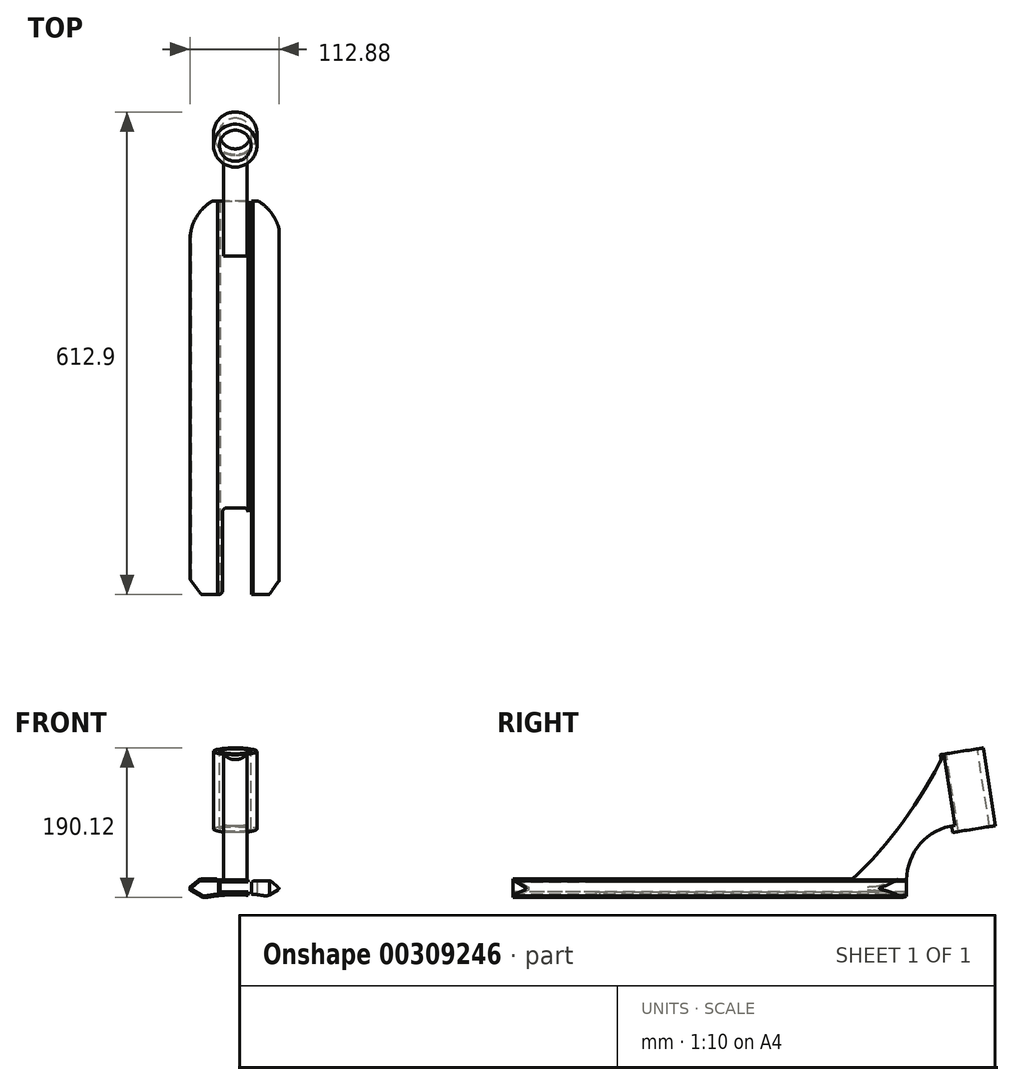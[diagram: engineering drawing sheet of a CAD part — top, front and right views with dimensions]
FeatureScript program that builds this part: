
annotation { "Feature Type Name" : "Feature", "Feature Type Description" : "" }
export const myFeature = defineFeature(function(context is Context, id is Id, definition is map)
    precondition{}
    {
        {
            var Q0;
            Q0=qCreatedBy(makeId("Front.planeOp"),FACE);
            var sketch = newSketch(context, id + "F0", { "sketchPlane" : qUnion([Q0])});
            skLineSegment(sketch, "E0", {"start": v(0, 0) * mm, "end": v(0, 5.19) * mm, "construction": true});
            skLineSegment(sketch, "E1", {"start": v(0, 3.89) * mm, "end": v(22.5, 3.89) * mm});
            skLineSegment(sketch, "E2", {"start": v(22.5, 3.89) * mm, "end": v(22.5, 5.19) * mm});
            skLineSegment(sketch, "E3", {"start": v(22.5, 5.19) * mm, "end": v(45.58, 5.19) * mm});
            skLineSegment(sketch, "E4", {"start": v(45.58, 5.19) * mm, "end": v(57.5, -4.81) * mm});
            skLineSegment(sketch, "E5", {"start": v(57.5, -4.81) * mm, "end": v(57.5, -8.81) * mm});
            skLineSegment(sketch, "E6", {"start": v(57.5, -8.81) * mm, "end": v(40.18, -18.81) * mm});
            skLineSegment(sketch, "E7.MirrorCS", {"start": v(0, 3.89) * mm, "end": v(-22.5, 3.89) * mm});
            skLineSegment(sketch, "E8.MirrorCS", {"start": v(-22.5, 3.89) * mm, "end": v(-22.5, 5.19) * mm});
            skLineSegment(sketch, "E9.MirrorCS", {"start": v(-22.5, 5.19) * mm, "end": v(-45.58, 5.19) * mm});
            skLineSegment(sketch, "E10.MirrorCS", {"start": v(-45.58, 5.19) * mm, "end": v(-57.5, -4.81) * mm});
            skLineSegment(sketch, "E11.MirrorCS", {"start": v(-57.5, -4.81) * mm, "end": v(-57.5, -8.81) * mm});
            skLineSegment(sketch, "E12.MirrorCS", {"start": v(-57.5, -8.81) * mm, "end": v(-40.18, -18.81) * mm});
            skArc(sketch, "E13", {"start": v(40.18, -18.81) * mm, "mid": v(0, -14.73) * mm, "end": v(-40.18, -18.81) * mm});
            skSolve(sketch);
        }
        {
            var Q0;
            Q0=makeQuery(id+"F0.imprint","IMPRINT",FACE,{"disambiguationData":[TD([[makeQuery(id+"F0.imprint","IMPRINT",EDGE,{"derivedFrom":sQuery(id+"F0.wireOp",EDGE,"E1")}),-1.0]])]});
            extrude(context, id + "F1", {"entities" : qUnion([Q0]), "endBound" : BoundingType.SYMMETRIC, "depth" : 500 * mm});
        }
        {
            var Q0;
            Q0=qCreatedBy(makeId("Front.planeOp"),FACE);
            var sketch = newSketch(context, id + "F2", { "sketchPlane" : qUnion([Q0])});
            skLineSegment(sketch, "E14.bottom", {"start": v(-19, 1.89) * mm, "end": v(19, 1.89) * mm});
            skLineSegment(sketch, "E14.top", {"start": v(-19, -11.11) * mm, "end": v(19, -11.11) * mm});
            skLineSegment(sketch, "E14.left", {"start": v(-19, 1.89) * mm, "end": v(-19, -11.11) * mm});
            skLineSegment(sketch, "E14.right", {"start": v(19, 1.89) * mm, "end": v(19, -11.11) * mm});
            skSolve(sketch);
        }
        {
            var Q0;
            Q0=makeQuery(id+"F1.opExtrude","SWEPT_EDGE",EDGE,{"disambiguationData":[OSD([sQuery(id+"F0.wireOp",EDGE,"E9.MirrorCS"),sQuery(id+"F0.wireOp",EDGE,"E10.MirrorCS")])]});
            var Q1;
            Q1=makeQuery(id+"F1.opExtrude","SWEPT_EDGE",EDGE,{"disambiguationData":[OSD([sQuery(id+"F0.wireOp",EDGE,"E3"),sQuery(id+"F0.wireOp",EDGE,"E4")])]});
            var Q2;
            Q2=makeQuery(id+"F1.opExtrude","SWEPT_EDGE",EDGE,{"disambiguationData":[OSD([sQuery(id+"F0.wireOp",EDGE,"E6"),sQuery(id+"F0.wireOp",EDGE,"E13")])]});
            var Q3;
            Q3=makeQuery(id+"F1.opExtrude","SWEPT_EDGE",EDGE,{"disambiguationData":[OSD([sQuery(id+"F0.wireOp",EDGE,"E12.MirrorCS"),sQuery(id+"F0.wireOp",EDGE,"E13")])]});
            fillet(context, id + "F3", {"entities" : qUnion([Q0, Q1, Q2, Q3]), "radius" : 9 * mm, "tangentPropagation" : true, "allowEdgeOverflow" : false});
        }
        {
            var Q0;
            Q0=makeQuery(id+"F1.opExtrude","SWEPT_EDGE",EDGE,{"disambiguationData":[OSD([sQuery(id+"F0.wireOp",EDGE,"E2"),sQuery(id+"F0.wireOp",EDGE,"E3")])]});
            var Q1;
            Q1=makeQuery(id+"F1.opExtrude","SWEPT_EDGE",EDGE,{"disambiguationData":[OSD([sQuery(id+"F0.wireOp",EDGE,"E8.MirrorCS"),sQuery(id+"F0.wireOp",EDGE,"E9.MirrorCS")])]});
            fillet(context, id + "F4", {"entities" : qUnion([Q0, Q1]), "radius" : 2 * mm, "tangentPropagation" : true, "allowEdgeOverflow" : false});
        }
        {
            var Q0;
            Q0=makeQuery(id+"F1.opExtrude","SWEPT_EDGE",EDGE,{"disambiguationData":[OSD([sQuery(id+"F0.wireOp",EDGE,"E5"),sQuery(id+"F0.wireOp",EDGE,"E6")])]});
            var Q1;
            Q1=makeQuery(id+"F1.opExtrude","SWEPT_EDGE",EDGE,{"disambiguationData":[OSD([sQuery(id+"F0.wireOp",EDGE,"E4"),sQuery(id+"F0.wireOp",EDGE,"E5")])]});
            var Q2;
            Q2=makeQuery(id+"F1.opExtrude","SWEPT_EDGE",EDGE,{"disambiguationData":[OSD([sQuery(id+"F0.wireOp",EDGE,"E11.MirrorCS"),sQuery(id+"F0.wireOp",EDGE,"E12.MirrorCS")])]});
            var Q3;
            Q3=makeQuery(id+"F1.opExtrude","SWEPT_EDGE",EDGE,{"disambiguationData":[OSD([sQuery(id+"F0.wireOp",EDGE,"E10.MirrorCS"),sQuery(id+"F0.wireOp",EDGE,"E11.MirrorCS")])]});
            fillet(context, id + "F5", {"entities" : qUnion([Q0, Q1, Q2, Q3]), "radius" : 1 * mm, "tangentPropagation" : true, "allowEdgeOverflow" : false});
        }
        {
            var Q0;
            Q0 = qSketchRegion(id + "F2", true);
            var Q1;
            Q1 = qSketchRegion(id + "F7", true);
            extrude(context, id + "F6", {"entities" : qUnion([Q0, Q1]), "operationType" : NewBodyOperationType.REMOVE, "endBound" : BoundingType.SYMMETRIC, "oppositeDirection" : true, "depth" : 500 * mm});
        }
        {
            var Q0;
            Q0=qCreatedBy(makeId("Top.planeOp"),FACE);
            var sketch = newSketch(context, id + "F7", { "sketchPlane" : qUnion([Q0])});
            skArc(sketch, "E15", {"start": v(57.5, 199.62) * mm, "mid": v(0.16, 257.5) * mm, "end": v(-57.5, 199.94) * mm});
            skLineSegment(sketch, "E16", {"start": v(-57.5, 199.94) * mm, "end": v(-57.5, 279.62) * mm});
            skLineSegment(sketch, "E17", {"start": v(57.5, 199.62) * mm, "end": v(57.5, 279.62) * mm});
            skLineSegment(sketch, "E18", {"start": v(57.5, 279.62) * mm, "end": v(-57.5, 279.62) * mm});
            skSolve(sketch);
        }
        {
            var Q0;
            {var subQ5=sQuery(id+"F7.wireOp",EDGE,"E18");Q0=makeQuery(id+"F7.imprint","IMPRINT",FACE,{"disambiguationData":[TD([[makeQuery(id+"F7.imprint","IMPRINT",EDGE,{"derivedFrom":subQ5}),1.0]])]});}
            extrude(context, id + "F8", {"entities" : qUnion([Q0]), "operationType" : NewBodyOperationType.REMOVE, "endBound" : BoundingType.THROUGH_ALL, "oppositeDirection" : true, "depth" : 25 * mm, "hasSecondDirection" : true, "secondDirectionBound" : SecondDirectionBoundingType.THROUGH_ALL, "secondDirectionOppositeDirection" : false, "secondDirectionDepth" : 25 * mm});
        }
        {
            var Q0;
            Q0=qCreatedBy(makeId("Top.planeOp"),FACE);
            var sketch = newSketch(context, id + "F9", { "sketchPlane" : qUnion([Q0])});
            skLineSegment(sketch, "E19", {"start": v(-16, -140) * mm, "end": v(16, -140) * mm});
            skLineSegment(sketch, "E20", {"start": v(16, -140) * mm, "end": v(16, -250) * mm});
            skLineSegment(sketch, "E21", {"start": v(-16, -140) * mm, "end": v(-16, -250) * mm});
            skLineSegment(sketch, "E22", {"start": v(-16, -250) * mm, "end": v(-43.3, -250) * mm});
            skLineSegment(sketch, "E23", {"start": v(-43.3, -250) * mm, "end": v(-68, -216) * mm});
            skLineSegment(sketch, "E24", {"start": v(-68, -216) * mm, "end": v(-68, -346) * mm});
            skLineSegment(sketch, "E25", {"start": v(-68, -346) * mm, "end": v(68, -346) * mm});
            skLineSegment(sketch, "E26", {"start": v(68, -346) * mm, "end": v(68, -216) * mm});
            skLineSegment(sketch, "E27", {"start": v(68, -216) * mm, "end": v(43.3, -250) * mm});
            skLineSegment(sketch, "E28", {"start": v(43.3, -250) * mm, "end": v(16, -250) * mm});
            skSolve(sketch);
        }
        {
            var Q0;
            Q0 = qSketchRegion(id + "F9", true);
            extrude(context, id + "F10", {"entities" : qUnion([Q0]), "operationType" : NewBodyOperationType.REMOVE, "endBound" : BoundingType.THROUGH_ALL, "depth" : 25 * mm, "hasSecondDirection" : true, "secondDirectionBound" : SecondDirectionBoundingType.THROUGH_ALL, "secondDirectionOppositeDirection" : true, "secondDirectionDepth" : 25 * mm});
        }
        {
            var Q0;
            {var subQ0=sQuery(id+"F9.wireOp",EDGE,"E19");var subQ1=sQuery(id+"F9.wireOp",EDGE,"E20");Q0=makeQuery(id+"F10.boolean.opBoolean","COPY",EDGE,{"disambiguationData":[TD([makeQuery(id+"F6.boolean.opBoolean","COPY",FACE,{"derivedFrom":makeQuery(id+"F6.opExtrude","SWEPT_FACE",FACE,{"disambiguationData":[OSD([sQuery(id+"F2.wireOp",EDGE,"E14.bottom")])]})})])],"derivedFrom":makeQuery(id+"F10.opExtrude","SWEPT_EDGE",EDGE,{"disambiguationData":[OSD([subQ0,subQ1])]})});}
            var Q1;
            {var subQ0=sQuery(id+"F9.wireOp",EDGE,"E19");var subQ1=sQuery(id+"F9.wireOp",EDGE,"E20");Q1=makeQuery(id+"F10.boolean.opBoolean","COPY",EDGE,{"disambiguationData":[TD([makeQuery(id+"F1.opExtrude","SWEPT_FACE",FACE,{"disambiguationData":[OSD([sQuery(id+"F0.wireOp",EDGE,"E13")])]})])],"derivedFrom":makeQuery(id+"F10.opExtrude","SWEPT_EDGE",EDGE,{"disambiguationData":[OSD([subQ0,subQ1])]})});}
            var Q2;
            {var subQ0=sQuery(id+"F9.wireOp",EDGE,"E19");var subQ1=sQuery(id+"F9.wireOp",EDGE,"E21");Q2=makeQuery(id+"F10.boolean.opBoolean","COPY",EDGE,{"disambiguationData":[TD([makeQuery(id+"F6.boolean.opBoolean","COPY",FACE,{"derivedFrom":makeQuery(id+"F6.opExtrude","SWEPT_FACE",FACE,{"disambiguationData":[OSD([sQuery(id+"F2.wireOp",EDGE,"E14.bottom")])]})})])],"derivedFrom":makeQuery(id+"F10.opExtrude","SWEPT_EDGE",EDGE,{"disambiguationData":[OSD([subQ0,subQ1])]})});}
            var Q3;
            {var subQ0=sQuery(id+"F9.wireOp",EDGE,"E19");var subQ1=sQuery(id+"F9.wireOp",EDGE,"E21");Q3=makeQuery(id+"F10.boolean.opBoolean","COPY",EDGE,{"disambiguationData":[TD([makeQuery(id+"F1.opExtrude","SWEPT_FACE",FACE,{"disambiguationData":[OSD([sQuery(id+"F0.wireOp",EDGE,"E13")])]})])],"derivedFrom":makeQuery(id+"F10.opExtrude","SWEPT_EDGE",EDGE,{"disambiguationData":[OSD([subQ0,subQ1])]})});}
            var Q4;
            {var subQ0=sQuery(id+"F9.wireOp",EDGE,"E21");Q4=makeQuery(id+"F10.boolean.opBoolean","COPY",EDGE,{"disambiguationData":[TD([makeQuery(id+"F1.opExtrude","SWEPT_FACE",FACE,{"disambiguationData":[OSD([sQuery(id+"F0.wireOp",EDGE,"E13")])]})])],"derivedFrom":makeQuery(id+"F10.opExtrude","SWEPT_EDGE",EDGE,{"disambiguationData":[OSD([subQ0,sQuery(id+"F9.wireOp",EDGE,"E22")])]})});}
            var Q5;
            {var subQ0=sQuery(id+"F9.wireOp",EDGE,"E20");Q5=makeQuery(id+"F10.boolean.opBoolean","COPY",EDGE,{"disambiguationData":[TD([makeQuery(id+"F6.boolean.opBoolean","COPY",FACE,{"derivedFrom":makeQuery(id+"F6.opExtrude","SWEPT_FACE",FACE,{"disambiguationData":[OSD([sQuery(id+"F2.wireOp",EDGE,"E14.bottom")])]})})])],"derivedFrom":makeQuery(id+"F10.opExtrude","SWEPT_EDGE",EDGE,{"disambiguationData":[OSD([subQ0,sQuery(id+"F9.wireOp",EDGE,"E28")])]})});}
            fillet(context, id + "F11", {"entities" : qUnion([Q0, Q1, Q2, Q3, Q4, Q5]), "radius" : 5 * mm, "tangentPropagation" : true, "allowEdgeOverflow" : false});
        }
        {
            var Q0;
            Q0=qCreatedBy(makeId("Right.planeOp"),FACE);
            var sketch = newSketch(context, id + "F12", { "sketchPlane" : qUnion([Q0])});
            skArc(sketch, "E29", {"start": v(180, 3.89) * mm, "mid": v(245.97, 78.55) * mm, "end": v(297.38, 163.89) * mm});
            skLineSegment(sketch, "E30", {"start": v(297.38, 163.89) * mm, "end": v(342.82, 171.08) * mm});
            skLineSegment(sketch, "E31", {"start": v(342.82, 171.08) * mm, "end": v(358.46, 72.32) * mm});
            skLineSegment(sketch, "E32", {"start": v(358.46, 72.32) * mm, "end": v(313.03, 65.12) * mm});
            skLineSegment(sketch, "E33", {"start": v(313.03, 65.12) * mm, "end": v(311.71, 73.4) * mm});
            skArc(sketch, "E34", {"start": v(311.71, 73.4) * mm, "mid": v(267.66, 50.36) * mm, "end": v(250, 3.89) * mm});
            skLineSegment(sketch, "E35", {"start": v(180, 3.89) * mm, "end": v(250, 3.89) * mm});
            skSolve(sketch);
        }
        {
            var Q0;
            Q0=makeQuery(id+"F12.imprint","IMPRINT",FACE,{"disambiguationData":[TD([[makeQuery(id+"F12.imprint","IMPRINT",EDGE,{"derivedFrom":sQuery(id+"F12.wireOp",EDGE,"E29")}),-1.0]])]});
            extrude(context, id + "F13", {"entities" : qUnion([Q0]), "operationType" : NewBodyOperationType.ADD, "endBound" : BoundingType.SYMMETRIC, "depth" : 30 * mm});
        }
        {
            var Q0;
            Q0=makeQuery(id+"F13.opExtrude","SWEPT_FACE",FACE,{"disambiguationData":[OSD([sQuery(id+"F12.wireOp",EDGE,"E30")])]});
            var sketch = newSketch(context, id + "F14", { "sketchPlane" : qUnion([Q0])});
            skCircle(sketch, "E36", {"center": v(0, 342.36) * mm, "radius": 27.5 * mm});
            skSolve(sketch);
        }
        {
            var Q0;
            Q0 = qSketchRegion(id + "F14", true);
            var Q1;
            Q1=makeQuery(id+"F13.opExtrude","SWEPT_FACE",FACE,{"disambiguationData":[OSD([sQuery(id+"F12.wireOp",EDGE,"E32")])]});
            extrude(context, id + "F15", {"entities" : qUnion([Q0]), "operationType" : NewBodyOperationType.ADD, "endBound" : BoundingType.UP_TO_SURFACE, "oppositeDirection" : true, "endBoundEntityFace" : qUnion([Q1]), "depth" : 25 * mm});
        }
        {
            var Q0;
            Q0=makeQuery(id+"F15.boolean.opBoolean","MERGE",FACE,{"derivedFrom":[makeQuery(id+"F13.opExtrude","SWEPT_FACE",FACE,{"disambiguationData":[OSD([sQuery(id+"F12.wireOp",EDGE,"E30")])]}),makeQuery(id+"F15.opExtrude","CAP_FACE",FACE,{"disambiguationData":[OSD([sQuery(id+"F14.wireOp",EDGE,"E36")])],"isStart":true})]});
            var sketch = newSketch(context, id + "F16", { "sketchPlane" : qUnion([Q0])});
            skPoint(sketch, "E37", {"position": v(0, 342.36) * mm});
            skSolve(sketch);
        }
        {
            var Q0;
            Q0=sQuery(id+"F16.wireOp",VERTEX,"E37");
            var Q1;
            Q1=makeQuery(id+"F1.opExtrude","SWEPT_BODY",BODY,{"disambiguationData":[OSD([sQuery(id+"F0.wireOp",EDGE,"E1"),sQuery(id+"F0.wireOp",EDGE,"E2"),sQuery(id+"F0.wireOp",EDGE,"E3"),sQuery(id+"F0.wireOp",EDGE,"E4"),sQuery(id+"F0.wireOp",EDGE,"E5"),sQuery(id+"F0.wireOp",EDGE,"E6"),sQuery(id+"F0.wireOp",EDGE,"E7.MirrorCS"),sQuery(id+"F0.wireOp",EDGE,"E8.MirrorCS"),sQuery(id+"F0.wireOp",EDGE,"E9.MirrorCS"),sQuery(id+"F0.wireOp",EDGE,"E10.MirrorCS"),sQuery(id+"F0.wireOp",EDGE,"E11.MirrorCS"),sQuery(id+"F0.wireOp",EDGE,"E12.MirrorCS"),sQuery(id+"F0.wireOp",EDGE,"E13")])]});
            hole(context, id + "F17", {"style" : HoleStyle.SIMPLE, "endStyle" : HoleEndStyle.THROUGH, "holeDiameter" : 40 * mm, "isTappedThrough" : true, "tappedDepth" : 12 * mm, "tapClearance" : 3, "locations" : qUnion([Q0]), "scope" : qUnion([Q1])});
        }
        {
            var Q0;
            Q0=makeQuery(id+"F1.opExtrude","CAP_FACE",FACE,{"disambiguationData":[OSD([sQuery(id+"F0.wireOp",EDGE,"E1"),sQuery(id+"F0.wireOp",EDGE,"E2"),sQuery(id+"F0.wireOp",EDGE,"E3"),sQuery(id+"F0.wireOp",EDGE,"E4"),sQuery(id+"F0.wireOp",EDGE,"E5"),sQuery(id+"F0.wireOp",EDGE,"E6"),sQuery(id+"F0.wireOp",EDGE,"E7.MirrorCS"),sQuery(id+"F0.wireOp",EDGE,"E8.MirrorCS"),sQuery(id+"F0.wireOp",EDGE,"E9.MirrorCS"),sQuery(id+"F0.wireOp",EDGE,"E10.MirrorCS"),sQuery(id+"F0.wireOp",EDGE,"E11.MirrorCS"),sQuery(id+"F0.wireOp",EDGE,"E12.MirrorCS"),sQuery(id+"F0.wireOp",EDGE,"E13")])],"isStart":false});
            var sketch = newSketch(context, id + "F18", { "sketchPlane" : qUnion([Q0])});
            skLineSegment(sketch, "E38.0.0", {"start": v(43.1, -17.12) * mm, "end": v(57, -9.1) * mm});
            skArc(sketch, "E38.0.1", {"start": v(57, -9.1) * mm, "mid": v(57.37, -8.73) * mm, "end": v(57.5, -8.23) * mm});
            skLineSegment(sketch, "E38.0.2", {"start": v(57.5, -8.23) * mm, "end": v(57.5, -5.28) * mm});
            skArc(sketch, "E38.0.3", {"start": v(57.5, -5.28) * mm, "mid": v(57.4, -4.86) * mm, "end": v(57.14, -4.51) * mm});
            skLineSegment(sketch, "E38.0.4", {"start": v(57.14, -4.51) * mm, "end": v(48.1, 3.08) * mm});
            skArc(sketch, "E38.0.5", {"start": v(48.1, 3.08) * mm, "mid": v(45.38, 4.65) * mm, "end": v(42.3, 5.19) * mm});
            skLineSegment(sketch, "E38.0.6", {"start": v(42.3, 5.19) * mm, "end": v(24.37, 5.19) * mm});
            skArc(sketch, "E38.0.7", {"start": v(24.37, 5.19) * mm, "mid": v(23.23, 4.83) * mm, "end": v(22.5, 3.89) * mm});
            skLineSegment(sketch, "E38.0.8", {"start": v(22.5, 3.89) * mm, "end": v(21, 3.89) * mm});
            skArc(sketch, "E38.0.9", {"start": v(-22.5, 3.89) * mm, "mid": v(-23.23, 4.83) * mm, "end": v(-24.37, 5.19) * mm});
            skLineSegment(sketch, "E38.0.10", {"start": v(-24.37, 5.19) * mm, "end": v(-42.3, 5.19) * mm});
            skArc(sketch, "E38.0.11", {"start": v(-42.3, 5.19) * mm, "mid": v(-45.38, 4.65) * mm, "end": v(-48.1, 3.08) * mm});
            skLineSegment(sketch, "E38.0.12", {"start": v(-48.1, 3.08) * mm, "end": v(-57.14, -4.51) * mm});
            skArc(sketch, "E38.0.13", {"start": v(-57.14, -4.51) * mm, "mid": v(-57.4, -4.86) * mm, "end": v(-57.5, -5.28) * mm});
            skLineSegment(sketch, "E38.0.14", {"start": v(-57.5, -5.28) * mm, "end": v(-57.5, -8.23) * mm});
            skArc(sketch, "E38.0.15", {"start": v(-57.5, -8.23) * mm, "mid": v(-57.37, -8.73) * mm, "end": v(-57, -9.1) * mm});
            skLineSegment(sketch, "E38.0.16", {"start": v(-57, -9.1) * mm, "end": v(-43.1, -17.12) * mm});
            skArc(sketch, "E38.0.17", {"start": v(-43.1, -17.12) * mm, "mid": v(-40.12, -18.2) * mm, "end": v(-36.94, -18.18) * mm});
            skArc(sketch, "E38.0.18", {"start": v(-36.94, -18.18) * mm, "mid": v(0, -14.73) * mm, "end": v(36.94, -18.18) * mm});
            skArc(sketch, "E38.0.19", {"start": v(36.94, -18.18) * mm, "mid": v(40.12, -18.2) * mm, "end": v(43.1, -17.12) * mm});
            skArc(sketch, "E39.0", {"start": v(-37.3, -16.2) * mm, "mid": v(-29.18, -14.85) * mm, "end": v(-21, -13.83) * mm});
            skArc(sketch, "E39.1", {"start": v(-42.1, -15.4) * mm, "mid": v(-39.78, -16.23) * mm, "end": v(-37.3, -16.2) * mm});
            skLineSegment(sketch, "E39.2", {"start": v(-24.37, 3.19) * mm, "end": v(-42.3, 3.19) * mm});
            skLineSegment(sketch, "E39.5", {"start": v(-54.38, -8.3) * mm, "end": v(-42.1, -15.4) * mm});
            skPoint(sketch, "E40.visualSharp", {"position": v(-56.85, -6.88) * mm});
            skArc(sketch, "E40.filletArc", {"start": v(-54.66, -5.04) * mm, "mid": v(-55.37, -6.75) * mm, "end": v(-54.38, -8.3) * mm});
            skLineSegment(sketch, "E41", {"start": v(-21, -13.83) * mm, "end": v(-21, 1.89) * mm});
            skLineSegment(sketch, "E42", {"start": v(-21, 1.89) * mm, "end": v(-22.5, 1.89) * mm});
            skArc(sketch, "E43.0", {"start": v(-42.3, 3.19) * mm, "mid": v(-44.7, 2.77) * mm, "end": v(-46.8, 1.55) * mm});
            skArc(sketch, "E44", {"start": v(-22.5, 1.89) * mm, "mid": v(-23.23, 2.83) * mm, "end": v(-24.37, 3.19) * mm});
            skLineSegment(sketch, "E45", {"start": v(-46.8, 1.55) * mm, "end": v(-54.66, -5.04) * mm});
            skLineSegment(sketch, "E46.MirrorCS", {"start": v(21, -13.83) * mm, "end": v(21, 1.89) * mm});
            skArc(sketch, "E47.MirrorCS", {"start": v(37.3, -16.2) * mm, "mid": v(29.18, -14.85) * mm, "end": v(21, -13.83) * mm});
            skArc(sketch, "E48.MirrorCS", {"start": v(42.1, -15.4) * mm, "mid": v(39.78, -16.23) * mm, "end": v(37.3, -16.2) * mm});
            skLineSegment(sketch, "E49.MirrorCS", {"start": v(54.38, -8.3) * mm, "end": v(42.1, -15.4) * mm});
            skArc(sketch, "E50.MirrorCS", {"start": v(54.66, -5.04) * mm, "mid": v(55.37, -6.75) * mm, "end": v(54.38, -8.3) * mm});
            skLineSegment(sketch, "E51.MirrorCS", {"start": v(46.8, 1.55) * mm, "end": v(54.66, -5.04) * mm});
            skArc(sketch, "E52.MirrorCS", {"start": v(42.3, 3.19) * mm, "mid": v(44.7, 2.77) * mm, "end": v(46.8, 1.55) * mm});
            skLineSegment(sketch, "E53.MirrorCS", {"start": v(24.37, 3.19) * mm, "end": v(42.3, 3.19) * mm});
            skArc(sketch, "E54.MirrorCS", {"start": v(22.5, 1.89) * mm, "mid": v(23.23, 2.83) * mm, "end": v(24.37, 3.19) * mm});
            skLineSegment(sketch, "E55.MirrorCS", {"start": v(21, 1.89) * mm, "end": v(22.5, 1.89) * mm});
            skArc(sketch, "E56.trimOffspring", {"start": v(-21, -13.83) * mm, "mid": v(-29.18, -14.85) * mm, "end": v(-37.3, -16.2) * mm});
            skArc(sketch, "E57.trimOffspring", {"start": v(21, -13.83) * mm, "mid": v(29.18, -14.85) * mm, "end": v(37.3, -16.2) * mm});
            skSolve(sketch);
        }
        {
            var Q0;
            Q0=makeQuery(id+"F18.imprint","IMPRINT",FACE,{"disambiguationData":[TD([[makeQuery(id+"F18.imprint","IMPRINT",EDGE,{"derivedFrom":sQuery(id+"F18.wireOp",EDGE,"E39.1")}),1.0]])]});
            var Q1;
            Q1=makeQuery(id+"F18.imprint","IMPRINT",FACE,{"disambiguationData":[TD([[makeQuery(id+"F18.imprint","IMPRINT",EDGE,{"derivedFrom":sQuery(id+"F18.wireOp",EDGE,"E46.MirrorCS")}),1.0]])]});
            var Q2;
            {var subQ4=sQuery(id+"F18.wireOp",EDGE,"E40.filletArc");Q2=makeQuery(id+"F18.imprint","IMPRINT",FACE,{"disambiguationData":[TD([[makeQuery(id+"F18.imprint","IMPRINT",EDGE,{"derivedFrom":subQ4}),1.0]])]});}
            var Q3;
            {var subQ1=sQuery(id+"F18.wireOp",EDGE,"E50.MirrorCS");Q3=makeQuery(id+"F18.imprint","IMPRINT",FACE,{"disambiguationData":[TD([[makeQuery(id+"F18.imprint","IMPRINT",EDGE,{"derivedFrom":subQ1}),-1.0]])]});}
            extrude(context, id + "F19", {"entities" : qUnion([Q0, Q1, Q2, Q3]), "operationType" : NewBodyOperationType.REMOVE, "depth" : 500 * mm, "hasSecondDirection" : true, "secondDirectionOppositeDirection" : true, "secondDirectionDepth" : 500 * mm});
        }
    });
